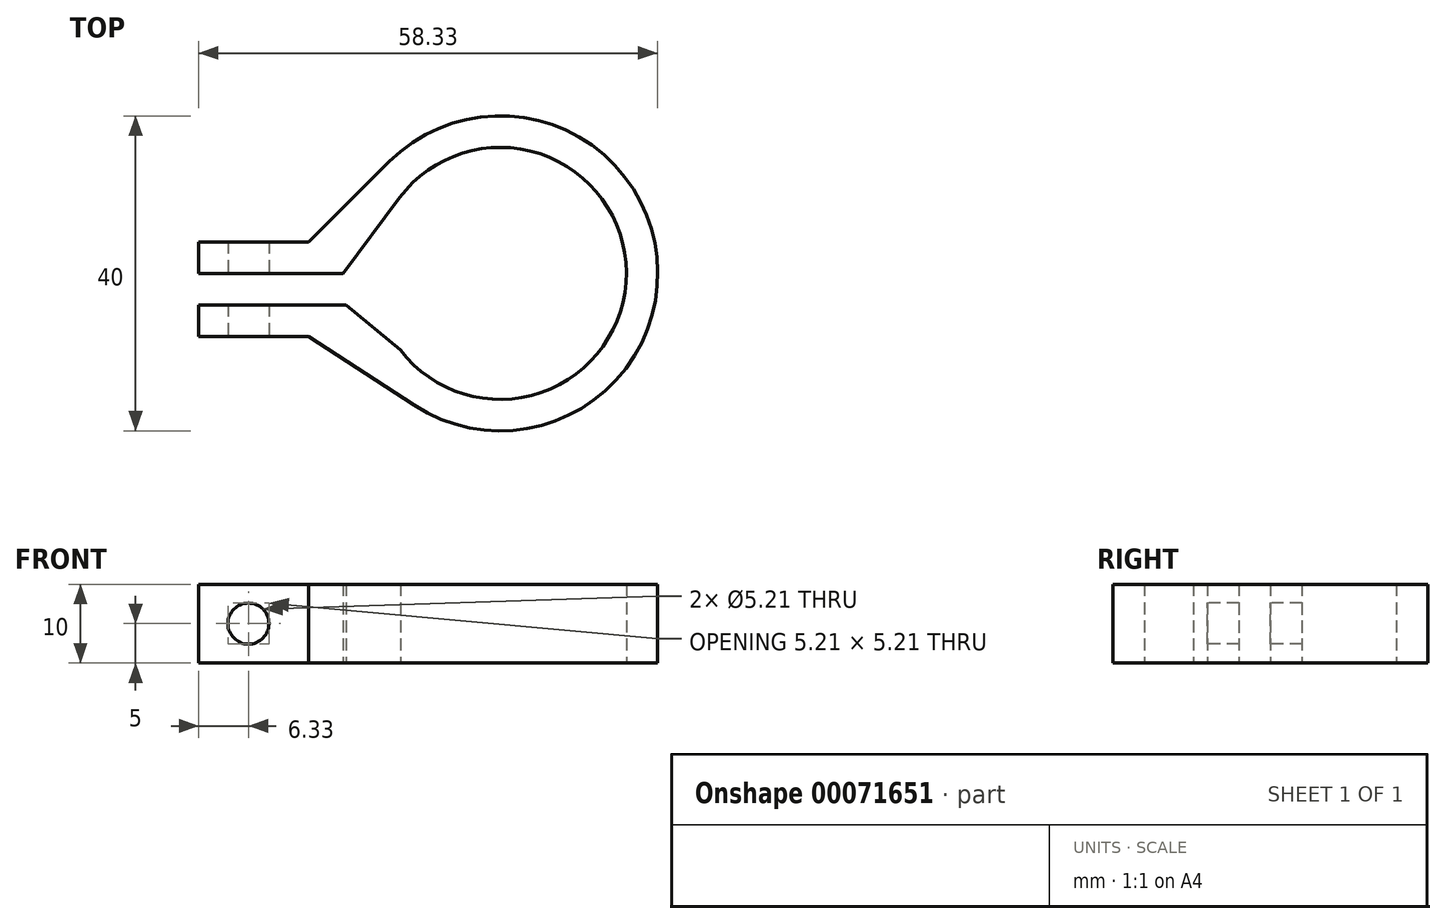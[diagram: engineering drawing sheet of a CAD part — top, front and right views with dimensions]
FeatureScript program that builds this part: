
annotation { "Feature Type Name" : "Feature", "Feature Type Description" : "" }
export const myFeature = defineFeature(function(context is Context, id is Id, definition is map)
    precondition{}
    {
        {
            var Q0;
            Q0=qCreatedBy(makeId("Top.planeOp"),FACE);
            var sketch = newSketch(context, id + "F0", { "sketchPlane" : qUnion([Q0])});
            skArc(sketch, "E0", {"start": v(-12.7, -9.74) * mm, "mid": v(16, 0.09) * mm, "end": v(-12.8, 9.6) * mm});
            skArc(sketch, "E1", {"start": v(-10.93, -16.75) * mm, "mid": v(19.9, 2.04) * mm, "end": v(-14.11, 14.17) * mm});
            skLineSegment(sketch, "E2", {"start": v(-24.33, -8) * mm, "end": v(-38.33, -8) * mm});
            skLineSegment(sketch, "E3", {"start": v(-38.33, -8) * mm, "end": v(-38.33, -4) * mm});
            skLineSegment(sketch, "E4", {"start": v(-38.33, -4) * mm, "end": v(-19.6, -4) * mm});
            skLineSegment(sketch, "E5", {"start": v(-20, 0) * mm, "end": v(-38.33, 0) * mm});
            skLineSegment(sketch, "E6", {"start": v(-38.33, 0) * mm, "end": v(-38.33, 4) * mm});
            skLineSegment(sketch, "E7", {"start": v(-38.33, 4) * mm, "end": v(-24.33, 4) * mm});
            skLineSegment(sketch, "E8", {"start": v(-24.33, 4) * mm, "end": v(-14.11, 14.17) * mm});
            skLineSegment(sketch, "E9", {"start": v(-24.33, -8) * mm, "end": v(-10.93, -16.75) * mm});
            skPoint(sketch, "E10.orphan", {"position": v(-18.33, -8) * mm});
            skLineSegment(sketch, "E11", {"start": v(-19.6, -4) * mm, "end": v(-12.7, -9.74) * mm});
            skLineSegment(sketch, "E12", {"start": v(-20, 0) * mm, "end": v(-12.8, 9.6) * mm});
            skSolve(sketch);
        }
        {
            var Q0;
            Q0=makeQuery(id+"F0.imprint","IMPRINT",FACE,{"disambiguationData":[TD([[makeQuery(id+"F0.imprint","IMPRINT",EDGE,{"derivedFrom":sQuery(id+"F0.wireOp",EDGE,"E0")}),-1.0]])]});
            extrude(context, id + "F1", {"entities" : qUnion([Q0]), "depth" : 10 * mm});
        }
        {
            var Q0;
            Q0=qCreatedBy(makeId("Front.planeOp"),FACE);
            var sketch = newSketch(context, id + "F2", { "sketchPlane" : qUnion([Q0])});
            skCircle(sketch, "E13", {"center": v(-32, 5) * mm, "radius": 2.6 * mm});
            skSolve(sketch);
        }
        {
            var Q0;
            Q0=makeQuery(id+"F2.imprint","IMPRINT",FACE,{"disambiguationData":[TD([[makeQuery(id+"F2.imprint","IMPRINT",EDGE,{"derivedFrom":sQuery(id+"F2.wireOp",EDGE,"E13")}),1.0]])]});
            extrude(context, id + "F3", {"entities" : qUnion([Q0]), "operationType" : NewBodyOperationType.REMOVE, "endBound" : BoundingType.SYMMETRIC, "oppositeDirection" : true, "depth" : 25 * mm});
        }
    });
